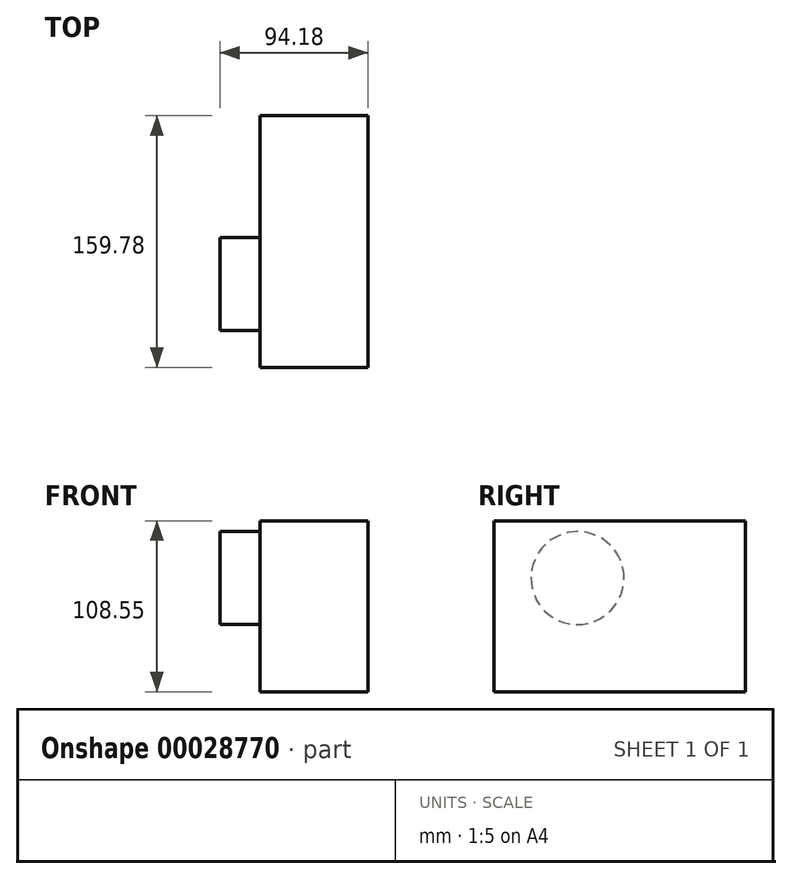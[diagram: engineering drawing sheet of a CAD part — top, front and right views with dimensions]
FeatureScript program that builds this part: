
annotation { "Feature Type Name" : "Feature", "Feature Type Description" : "" }
export const myFeature = defineFeature(function(context is Context, id is Id, definition is map)
    precondition{}
    {
        {
            var Q0;
            Q0=qCreatedBy(makeId("Front.planeOp"),FACE);
            var sketch = newSketch(context, id + "F0", { "sketchPlane" : qUnion([Q0])});
            skLineSegment(sketch, "E0.bottom", {"start": v(27.66, -44.72) * mm, "end": v(-41.12, -44.72) * mm});
            skLineSegment(sketch, "E0.top", {"start": v(27.66, 63.83) * mm, "end": v(-41.12, 63.83) * mm});
            skLineSegment(sketch, "E0.left", {"start": v(27.66, -44.72) * mm, "end": v(27.66, 63.83) * mm});
            skLineSegment(sketch, "E0.right", {"start": v(-41.12, -44.72) * mm, "end": v(-41.12, 63.83) * mm});
            skSolve(sketch);
        }
        {
            var Q0;
            Q0=makeQuery(id+"F0.imprint","IMPRINT",FACE,{"disambiguationData":[TD([[makeQuery(id+"F0.imprint","IMPRINT",EDGE,{"derivedFrom":sQuery(id+"F0.wireOp",EDGE,"E0.bottom")}),-1.0]])]});
            extrude(context, id + "F1", {"entities" : qUnion([Q0]), "depth" : 159.78 * mm});
        }
        {
            var Q0;
            Q0=makeQuery(id+"F1.opExtrude","SWEPT_FACE",FACE,{"disambiguationData":[OSD([sQuery(id+"F0.wireOp",EDGE,"E0.right")])]});
            var sketch = newSketch(context, id + "F2", { "sketchPlane" : qUnion([Q0])});
            skCircle(sketch, "E1", {"center": v(106.76, 27.48) * mm, "radius": 29.5 * mm});
            skSolve(sketch);
        }
        {
            var Q0;
            Q0=makeQuery(id+"F2.imprint","IMPRINT",FACE,{"disambiguationData":[TD([[makeQuery(id+"F2.imprint","IMPRINT",EDGE,{"derivedFrom":sQuery(id+"F2.wireOp",EDGE,"E1")}),1.0]])]});
            extrude(context, id + "F3", {"entities" : qUnion([Q0]), "operationType" : NewBodyOperationType.ADD, "depth" : 25.4 * mm});
        }
    });
